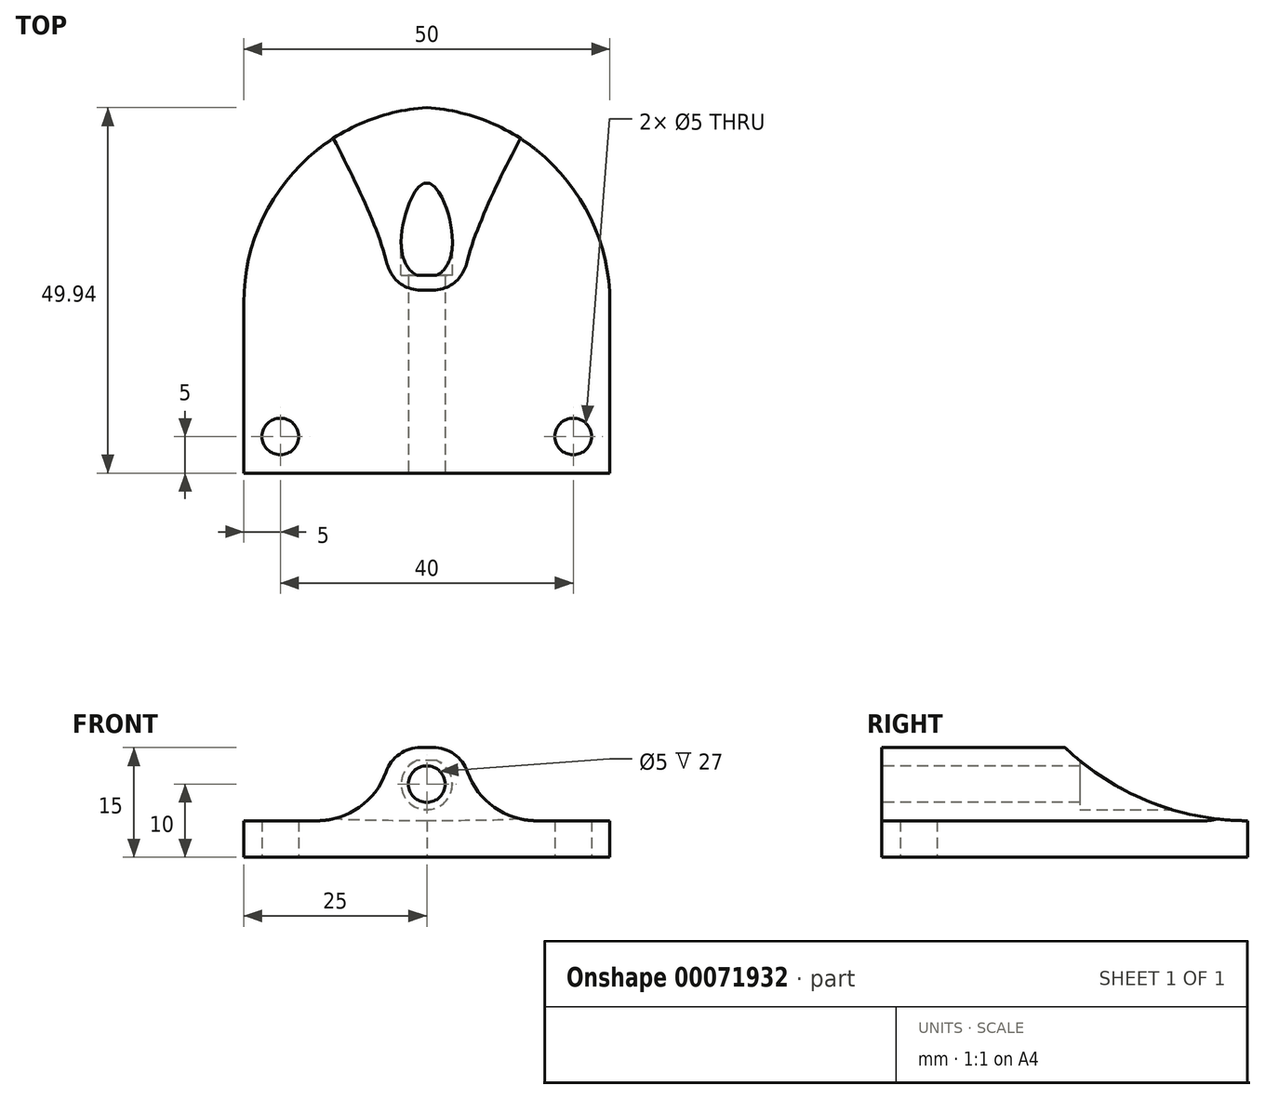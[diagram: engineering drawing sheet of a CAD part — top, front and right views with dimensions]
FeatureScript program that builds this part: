
annotation { "Feature Type Name" : "Feature", "Feature Type Description" : "" }
export const myFeature = defineFeature(function(context is Context, id is Id, definition is map)
    precondition{}
    {
        {
            var Q0;
            Q0=qCreatedBy(makeId("Top.planeOp"),FACE);
            var sketch = newSketch(context, id + "F0", { "sketchPlane" : qUnion([Q0])});
            skLineSegment(sketch, "E0.rect.bottom", {"start": v(25, -25) * mm, "end": v(-25, -25) * mm});
            skLineSegment(sketch, "E0.rect.top", {"start": v(25, 25) * mm, "end": v(-25, 25) * mm});
            skLineSegment(sketch, "E0.rect.left", {"start": v(25, -25) * mm, "end": v(25, 25) * mm});
            skLineSegment(sketch, "E0.rect.right", {"start": v(-25, -25) * mm, "end": v(-25, 25) * mm});
            skPoint(sketch, "E0.rect.middle", {"position": v(0, 0) * mm});
            skLineSegment(sketch, "E1", {"start": v(-20, -25) * mm, "end": v(-20, 25) * mm, "construction": true});
            skLineSegment(sketch, "E2", {"start": v(20, -25) * mm, "end": v(20, 25) * mm, "construction": true});
            skLineSegment(sketch, "E3", {"start": v(-25, -20) * mm, "end": v(25, -20) * mm, "construction": true});
            skCircle(sketch, "E4", {"center": v(-20, -20) * mm, "radius": 2.5 * mm});
            skCircle(sketch, "E5", {"center": v(20, -20) * mm, "radius": 2.5 * mm});
            skSolve(sketch);
        }
        {
            var Q0;
            Q0=makeQuery(id+"F0.imprint","IMPRINT",FACE,{"disambiguationData":[TD([[makeQuery(id+"F0.imprint","IMPRINT",EDGE,{"derivedFrom":sQuery(id+"F0.wireOp",EDGE,"E0.rect.bottom")}),-1.0]])]});
            extrude(context, id + "F1", {"entities" : qUnion([Q0]), "depth" : 5 * mm});
        }
        {
            var Q0;
            Q0=makeQuery(id+"F1.opExtrude","SWEPT_FACE",FACE,{"disambiguationData":[OSD([sQuery(id+"F0.wireOp",EDGE,"E0.rect.bottom")])]});
            var sketch = newSketch(context, id + "F2", { "sketchPlane" : qUnion([Q0])});
            skLineSegment(sketch, "E6", {"start": v(0, 0) * mm, "end": v(0, 20) * mm, "construction": true});
            skPoint(sketch, "E6.endSnap0", {"position": v(0, 5) * mm});
            skLineSegment(sketch, "E7", {"start": v(-25.12, 10) * mm, "end": v(24.95, 10) * mm, "construction": true});
            skPoint(sketch, "E7.startSnap0", {"position": v(0, 10) * mm});
            skLineSegment(sketch, "E8", {"start": v(-25.12, 5) * mm, "end": v(24.77, 5) * mm, "construction": true});
            skLineSegment(sketch, "E9", {"start": v(-25.21, 15) * mm, "end": v(25.66, 15) * mm, "construction": true});
            skCircle(sketch, "E10", {"center": v(0, 10) * mm, "radius": 2.5 * mm});
            skLineSegment(sketch, "E11.rect.bottom", {"start": v(5, 5) * mm, "end": v(-5, 5) * mm});
            skLineSegment(sketch, "E11.rect.top", {"start": v(5, 15) * mm, "end": v(-5, 15) * mm});
            skArc(sketch, "E12", {"start": v(-15, 5) * mm, "mid": v(-7.93, 7.93) * mm, "end": v(-5, 15) * mm});
            skArc(sketch, "E13.MirrorCS", {"start": v(15, 5) * mm, "mid": v(7.93, 7.93) * mm, "end": v(5, 15) * mm});
            skLineSegment(sketch, "E14", {"start": v(-15, 5) * mm, "end": v(-5, 5) * mm});
            skLineSegment(sketch, "E15", {"start": v(5, 5) * mm, "end": v(15, 5) * mm});
            skSolve(sketch);
        }
        {
            var Q0;
            Q0=makeQuery(id+"F2.imprint","IMPRINT",FACE,{"disambiguationData":[TD([[makeQuery(id+"F2.imprint","IMPRINT",EDGE,{"derivedFrom":sQuery(id+"F2.wireOp",EDGE,"E10")}),-1.0]])]});
            var Q1;
            Q1=makeQuery(id+"F1.opExtrude","SWEPT_FACE",FACE,{"disambiguationData":[OSD([sQuery(id+"F0.wireOp",EDGE,"E0.rect.top")])]});
            extrude(context, id + "F3", {"entities" : qUnion([Q0]), "operationType" : NewBodyOperationType.ADD, "endBound" : BoundingType.UP_TO_SURFACE, "oppositeDirection" : true, "endBoundEntityFace" : qUnion([Q1]), "depth" : 25 * mm});
        }
        {
            var Q0;
            Q0=makeQuery(id+"F3.opExtrude","SWEPT_EDGE",EDGE,{"disambiguationData":[OSD([sQuery(id+"F2.wireOp",EDGE,"E11.rect.top"),sQuery(id+"F2.wireOp",EDGE,"E12")])]});
            var Q1;
            Q1=makeQuery(id+"F3.opExtrude","SWEPT_EDGE",EDGE,{"disambiguationData":[OSD([sQuery(id+"F2.wireOp",EDGE,"E11.rect.top"),sQuery(id+"F2.wireOp",EDGE,"E13.MirrorCS")])]});
            fillet(context, id + "F4", {"entities" : qUnion([Q0, Q1]), "radius" : 5 * mm, "tangentPropagation" : true, "allowEdgeOverflow" : false});
        }
        {
            var Q0;
            Q0=makeQuery(id+"F1.opExtrude","SWEPT_FACE",FACE,{"disambiguationData":[OSD([sQuery(id+"F0.wireOp",EDGE,"E0.rect.right")])]});
            var sketch = newSketch(context, id + "F5", { "sketchPlane" : qUnion([Q0])});
            skLineSegment(sketch, "E16", {"start": v(-25, 15) * mm, "end": v(25, 15) * mm, "construction": true});
            skArc(sketch, "E17", {"start": v(-25, 5) * mm, "mid": v(-11.54, 7.6) * mm, "end": v(0, 15) * mm});
            skLineSegment(sketch, "E18", {"start": v(-25, 5) * mm, "end": v(-25, 15) * mm});
            skLineSegment(sketch, "E19", {"start": v(-25, 15) * mm, "end": v(0, 15) * mm});
            skSolve(sketch);
        }
        {
            var Q0;
            Q0=makeQuery(id+"F5.imprint","IMPRINT",FACE,{"disambiguationData":[TD([[makeQuery(id+"F5.imprint","IMPRINT",EDGE,{"derivedFrom":sQuery(id+"F5.wireOp",EDGE,"E17")}),1.0]])]});
            var Q1;
            Q1=makeQuery(id+"F1.opExtrude","SWEPT_FACE",FACE,{"disambiguationData":[OSD([sQuery(id+"F0.wireOp",EDGE,"E0.rect.left")])]});
            extrude(context, id + "F6", {"entities" : qUnion([Q0]), "operationType" : NewBodyOperationType.REMOVE, "endBound" : BoundingType.UP_TO_SURFACE, "oppositeDirection" : true, "endBoundEntityFace" : qUnion([Q1]), "depth" : 25 * mm});
        }
        {
            var Q0;
            Q0=makeQuery(id+"F3.boolean.opBoolean","MERGE",FACE,{"derivedFrom":[makeQuery(id+"F1.opExtrude","SWEPT_FACE",FACE,{"disambiguationData":[OSD([sQuery(id+"F0.wireOp",EDGE,"E0.rect.top")])]}),makeQuery(id+"F3.opExtrude","CAP_FACE",FACE,{"disambiguationData":[OSD([sQuery(id+"F2.wireOp",EDGE,"E10"),sQuery(id+"F2.wireOp",EDGE,"E11.rect.bottom"),sQuery(id+"F2.wireOp",EDGE,"E11.rect.top"),sQuery(id+"F2.wireOp",EDGE,"E12"),sQuery(id+"F2.wireOp",EDGE,"E13.MirrorCS"),sQuery(id+"F2.wireOp",EDGE,"E14"),sQuery(id+"F2.wireOp",EDGE,"E15")])],"isStart":false})]});
            var sketch = newSketch(context, id + "F7", { "sketchPlane" : qUnion([Q0])});
            skCircle(sketch, "E20", {"center": v(0, 10) * mm, "radius": 3.5 * mm});
            skSolve(sketch);
        }
        {
            var Q0;
            Q0=makeQuery(id+"F7.imprint","IMPRINT",FACE,{"disambiguationData":[TD([[makeQuery(id+"F7.imprint","IMPRINT",EDGE,{"derivedFrom":sQuery(id+"F7.wireOp",EDGE,"E20")}),1.0]])]});
            var Q1;
            Q1=sQuery(id+"F7.wireOp",EDGE,"E20");
            extrude(context, id + "F8", {"entities" : qUnion([Q0]), "operationType" : NewBodyOperationType.REMOVE, "surfaceEntities" : qUnion([Q1]), "oppositeDirection" : true, "depth" : 23 * mm});
        }
        {
            var Q0;
            Q0=makeQuery(id+"F1.opExtrude","SWEPT_EDGE",EDGE,{"disambiguationData":[OSD([sQuery(id+"F0.wireOp",EDGE,"E0.rect.top"),sQuery(id+"F0.wireOp",EDGE,"E0.rect.left")])]});
            var Q1;
            Q1=makeQuery(id+"F1.opExtrude","SWEPT_EDGE",EDGE,{"disambiguationData":[OSD([sQuery(id+"F0.wireOp",EDGE,"E0.rect.top"),sQuery(id+"F0.wireOp",EDGE,"E0.rect.right")])]});
            fillet(context, id + "F9", {"entities" : qUnion([Q0, Q1]), "radius" : 26.72 * mm, "tangentPropagation" : true, "allowEdgeOverflow" : false});
        }
    });
